# Revit family: RN 90097 Optifitt-Serra-Gewindeflansch PN 16
name_source: partatom
category: Rohrformteile
units: mm (PartAtom-declared; Revit-internal decimal feet)

## family parameters
Arbeitsebenenbasiert = Nein
Beim Laden mit Abzugskörper schneiden = Nein
Bemaßung runder Anschluss = Durchmesser verwenden
Gemeinsam genutzt = Nein
Immer vertikal = Ja
Teiletyp = Verbindung

## types (8) — shared parameters
1.010.00.2 Blattnummer der Richtlinie = 29
1.010.00.3 Ausgabedatum (Monat) der Richtlinie = 201308
1.010.00.4 Herstellername = R. Nussbaum AG
1.010.00.5 Revisionsdatum der Datei = 20190521
1.010.00.6 Webadresse des Herstellers = http://www.nussbaum.ch
1.100.00.4 Produktbezeichnung = Versorgung
1.110.00.2 Index = 3
1.110.00.4 Produktbezeichnung = Optifitt-Serra
1.960/3L.00.8 Link (URL) = https://www.nussbaum.ch
29.700.00.4 Produktname = Optifitt-Serra-Gewindeflansch PN 16
29.700.00.5 Produktkennung = 2
29.700.00.6 Querschnittsform = 1
29.700.00.7 Nennweitensystem = DN
29.700.00.8 Nenndrucksystem = PN
29.710.02.4 Nenndruck = 16
29.710.02.5 max. zul. Überdruck [hPa] = 1600
29.710.02.7 max. zul. Dauer-Betriebsdruck [hPa] = 1600
29.710.02.9 max. zul. Dauer-Betriebstemperatur [°C] = 90
Connector Visibility = Nein
EnclosingSpace Visibility = Nein
Hersteller = R. Nussbaum AG
URL = https://www.nussbaum.ch

## per-type parameters (varying)
- DN=80: 1.800.00.3 TGA-Nummer=01900300000000000000000000000000000000000000000034???000000000000008; 1.800.00.4 Kommentarfeld=90097.28, Optifitt-Serra-Gewindeflansch PN 16, DN=80, Rp=3; 1.810.00.3 Hersteller-Bestellnummer=90097.28; 1.810.00.4 DATANORM-Nummer=90097.28; 1.810.00.5 StLB-Nummer=216.641; 1.810.00.6 GTIN-Nummer=7612945680839; 29.710.02.10 Formstück-Gewicht [kg]=4.098; 29.710.02.3 Benennung=Optifitt-Serra-Gewindeflansch PN 16, DN=80, Rp=3; CONNECTOR0_DIAMETER_dX_0r=80 mm; CONNECTOR0_dX_01=30 mm; CONNECTOR0_ref_dX=30 mm; CONNECTOR1_DIAMETER_dX_0r=80 mm; CONNECTOR1_dX_00=34 mm; CONNECTOR1_dX_01=35 mm; CONNECTOR1_ref_dX=35 mm; Modell=90097.28; R. Nussbaum AG 90097.21 de Visibility=Nein; R. Nussbaum AG 90097.22 de Visibility=Nein; R. Nussbaum AG 90097.23 de Visibility=Nein; R. Nussbaum AG 90097.24 de Visibility=Nein; R. Nussbaum AG 90097.25 de Visibility=Nein; R. Nussbaum AG 90097.26 de Visibility=Nein; R. Nussbaum AG 90097.27 de Visibility=Nein; R. Nussbaum AG 90097.28 de Visibility=Ja; Typenkommentare=Optifitt-Serra-Gewindeflansch PN 16  DN=80
- DN=65: 1.800.00.3 TGA-Nummer=01900300000000000000000000000000000000000000000034???000000000000007; 1.800.00.4 Kommentarfeld=90097.27, Optifitt-Serra-Gewindeflansch PN 16, DN=65, Rp=2½; 1.810.00.3 Hersteller-Bestellnummer=90097.27; 1.810.00.4 DATANORM-Nummer=90097.27; 1.810.00.5 StLB-Nummer=216.638; 1.810.00.6 GTIN-Nummer=7612945680822; 29.710.02.10 Formstück-Gewicht [kg]=3.335; 29.710.02.3 Benennung=Optifitt-Serra-Gewindeflansch PN 16, DN=65, Rp=2½; CONNECTOR0_DIAMETER_dX_0r=65 mm; CONNECTOR0_dX_01=27 mm; CONNECTOR0_ref_dX=27 mm; CONNECTOR1_DIAMETER_dX_0r=65 mm; CONNECTOR1_dX_00=32 mm; CONNECTOR1_dX_01=33 mm; CONNECTOR1_ref_dX=33 mm; Modell=90097.27; R. Nussbaum AG 90097.21 de Visibility=Nein; R. Nussbaum AG 90097.22 de Visibility=Nein; R. Nussbaum AG 90097.23 de Visibility=Nein; R. Nussbaum AG 90097.24 de Visibility=Nein; R. Nussbaum AG 90097.25 de Visibility=Nein; R. Nussbaum AG 90097.26 de Visibility=Nein; R. Nussbaum AG 90097.27 de Visibility=Ja; R. Nussbaum AG 90097.28 de Visibility=Nein; Typenkommentare=Optifitt-Serra-Gewindeflansch PN 16  DN=65
- DN=50: 1.800.00.3 TGA-Nummer=01900300000000000000000000000000000000000000000034???000000000000006; 1.800.00.4 Kommentarfeld=90097.26, Optifitt-Serra-Gewindeflansch PN 16, DN=50, Rp=2; 1.810.00.3 Hersteller-Bestellnummer=90097.26; 1.810.00.4 DATANORM-Nummer=90097.26; 1.810.00.5 StLB-Nummer=216.637; 1.810.00.6 GTIN-Nummer=7612945680815; 29.710.02.10 Formstück-Gewicht [kg]=2.579; 29.710.02.3 Benennung=Optifitt-Serra-Gewindeflansch PN 16, DN=50, Rp=2; CONNECTOR0_DIAMETER_dX_0r=50 mm; CONNECTOR0_dX_01=24 mm; CONNECTOR0_ref_dX=24 mm; CONNECTOR1_DIAMETER_dX_0r=50 mm; CONNECTOR1_dX_00=28 mm; CONNECTOR1_dX_01=29 mm; CONNECTOR1_ref_dX=29 mm; Modell=90097.26; R. Nussbaum AG 90097.21 de Visibility=Nein; R. Nussbaum AG 90097.22 de Visibility=Nein; R. Nussbaum AG 90097.23 de Visibility=Nein; R. Nussbaum AG 90097.24 de Visibility=Nein; R. Nussbaum AG 90097.25 de Visibility=Nein; R. Nussbaum AG 90097.26 de Visibility=Ja; R. Nussbaum AG 90097.27 de Visibility=Nein; R. Nussbaum AG 90097.28 de Visibility=Nein; Typenkommentare=Optifitt-Serra-Gewindeflansch PN 16  DN=50
- DN=40: 1.800.00.3 TGA-Nummer=01900300000000000000000000000000000000000000000034???000000000000005; 1.800.00.4 Kommentarfeld=90097.25, Optifitt-Serra-Gewindeflansch PN 16, DN=40, Rp=1½; 1.810.00.3 Hersteller-Bestellnummer=90097.25; 1.810.00.4 DATANORM-Nummer=90097.25; 1.810.00.5 StLB-Nummer=216.636; 1.810.00.6 GTIN-Nummer=7612945680808; 29.710.02.10 Formstück-Gewicht [kg]=2.219; 29.710.02.3 Benennung=Optifitt-Serra-Gewindeflansch PN 16, DN=40, Rp=1½; CONNECTOR0_DIAMETER_dX_0r=40 mm; CONNECTOR0_dX_01=19 mm; CONNECTOR0_ref_dX=19 mm; CONNECTOR1_DIAMETER_dX_0r=40 mm; CONNECTOR1_dX_00=32 mm; CONNECTOR1_dX_01=33 mm; CONNECTOR1_ref_dX=33 mm; Modell=90097.25; R. Nussbaum AG 90097.21 de Visibility=Nein; R. Nussbaum AG 90097.22 de Visibility=Nein; R. Nussbaum AG 90097.23 de Visibility=Nein; R. Nussbaum AG 90097.24 de Visibility=Nein; R. Nussbaum AG 90097.25 de Visibility=Ja; R. Nussbaum AG 90097.26 de Visibility=Nein; R. Nussbaum AG 90097.27 de Visibility=Nein; R. Nussbaum AG 90097.28 de Visibility=Nein; Typenkommentare=Optifitt-Serra-Gewindeflansch PN 16  DN=40
- DN=32: 1.800.00.3 TGA-Nummer=01900300000000000000000000000000000000000000000034???000000000000004; 1.800.00.4 Kommentarfeld=90097.24, Optifitt-Serra-Gewindeflansch PN 16, DN=32, Rp=1¼; 1.810.00.3 Hersteller-Bestellnummer=90097.24; 1.810.00.4 DATANORM-Nummer=90097.24; 1.810.00.5 StLB-Nummer=216.635; 1.810.00.6 GTIN-Nummer=7612945680792; 29.710.02.10 Formstück-Gewicht [kg]=1.959; 29.710.02.3 Benennung=Optifitt-Serra-Gewindeflansch PN 16, DN=32, Rp=1¼; CONNECTOR0_DIAMETER_dX_0r=32 mm; CONNECTOR0_dX_01=19 mm; CONNECTOR0_ref_dX=19 mm; CONNECTOR1_DIAMETER_dX_0r=32 mm; CONNECTOR1_dX_00=26 mm; CONNECTOR1_dX_01=27 mm; CONNECTOR1_ref_dX=27 mm; Modell=90097.24; R. Nussbaum AG 90097.21 de Visibility=Nein; R. Nussbaum AG 90097.22 de Visibility=Nein; R. Nussbaum AG 90097.23 de Visibility=Nein; R. Nussbaum AG 90097.24 de Visibility=Ja; R. Nussbaum AG 90097.25 de Visibility=Nein; R. Nussbaum AG 90097.26 de Visibility=Nein; R. Nussbaum AG 90097.27 de Visibility=Nein; R. Nussbaum AG 90097.28 de Visibility=Nein; Typenkommentare=Optifitt-Serra-Gewindeflansch PN 16  DN=32
- DN=25: 1.800.00.3 TGA-Nummer=01900300000000000000000000000000000000000000000034???000000000000003; 1.800.00.4 Kommentarfeld=90097.23, Optifitt-Serra-Gewindeflansch PN 16, DN=25, Rp=1; 1.810.00.3 Hersteller-Bestellnummer=90097.23; 1.810.00.4 DATANORM-Nummer=90097.23; 1.810.00.5 StLB-Nummer=216.634; 1.810.00.6 GTIN-Nummer=7612945680785; 29.710.02.10 Formstück-Gewicht [kg]=1.325; 29.710.02.3 Benennung=Optifitt-Serra-Gewindeflansch PN 16, DN=25, Rp=1; CONNECTOR0_DIAMETER_dX_0r=25 mm  [stored 0.082021 ft]; CONNECTOR0_dX_01=17 mm; CONNECTOR0_ref_dX=17 mm; CONNECTOR1_DIAMETER_dX_0r=25 mm  [stored 0.082021 ft]; CONNECTOR1_dX_00=24 mm; CONNECTOR1_dX_01=25 mm  [stored 0.082021 ft]; CONNECTOR1_ref_dX=25 mm  [stored 0.082021 ft]; Modell=90097.23; R. Nussbaum AG 90097.21 de Visibility=Nein; R. Nussbaum AG 90097.22 de Visibility=Nein; R. Nussbaum AG 90097.23 de Visibility=Ja; R. Nussbaum AG 90097.24 de Visibility=Nein; R. Nussbaum AG 90097.25 de Visibility=Nein; R. Nussbaum AG 90097.26 de Visibility=Nein; R. Nussbaum AG 90097.27 de Visibility=Nein; R. Nussbaum AG 90097.28 de Visibility=Nein; Typenkommentare=Optifitt-Serra-Gewindeflansch PN 16  DN=25
- DN=20: 1.800.00.3 TGA-Nummer=01900300000000000000000000000000000000000000000034???000000000000002; 1.800.00.4 Kommentarfeld=90097.22, Optifitt-Serra-Gewindeflansch PN 16, DN=20, Rp=¾; 1.810.00.3 Hersteller-Bestellnummer=90097.22; 1.810.00.4 DATANORM-Nummer=90097.22; 1.810.00.5 StLB-Nummer=216.633; 1.810.00.6 GTIN-Nummer=7612945680778; 29.710.02.10 Formstück-Gewicht [kg]=0.929; 29.710.02.3 Benennung=Optifitt-Serra-Gewindeflansch PN 16, DN=20, Rp=¾; CONNECTOR0_DIAMETER_dX_0r=20 mm; CONNECTOR0_dX_01=15 mm; CONNECTOR0_ref_dX=15 mm; CONNECTOR1_DIAMETER_dX_0r=20 mm; CONNECTOR1_dX_00=24 mm; CONNECTOR1_dX_01=25 mm  [stored 0.082021 ft]; CONNECTOR1_ref_dX=25 mm  [stored 0.082021 ft]; Modell=90097.22; R. Nussbaum AG 90097.21 de Visibility=Nein; R. Nussbaum AG 90097.22 de Visibility=Ja; R. Nussbaum AG 90097.23 de Visibility=Nein; R. Nussbaum AG 90097.24 de Visibility=Nein; R. Nussbaum AG 90097.25 de Visibility=Nein; R. Nussbaum AG 90097.26 de Visibility=Nein; R. Nussbaum AG 90097.27 de Visibility=Nein; R. Nussbaum AG 90097.28 de Visibility=Nein; Typenkommentare=Optifitt-Serra-Gewindeflansch PN 16  DN=20
- DN=15: 1.800.00.3 TGA-Nummer=01900300000000000000000000000000000000000000000034???000000000000001; 1.800.00.4 Kommentarfeld=90097.21, Optifitt-Serra-Gewindeflansch PN 16, DN=15, Rp=½; 1.810.00.3 Hersteller-Bestellnummer=90097.21; 1.810.00.4 DATANORM-Nummer=90097.21; 1.810.00.5 StLB-Nummer=216.632; 1.810.00.6 GTIN-Nummer=7612945680761; 29.710.02.10 Formstück-Gewicht [kg]=0.779; 29.710.02.3 Benennung=Optifitt-Serra-Gewindeflansch PN 16, DN=15, Rp=½; CONNECTOR0_DIAMETER_dX_0r=15 mm; CONNECTOR0_dX_01=13 mm; CONNECTOR0_ref_dX=13 mm; CONNECTOR1_DIAMETER_dX_0r=15 mm; CONNECTOR1_dX_00=20 mm; CONNECTOR1_dX_01=21 mm; CONNECTOR1_ref_dX=21 mm; Modell=90097.21; R. Nussbaum AG 90097.21 de Visibility=Ja; R. Nussbaum AG 90097.22 de Visibility=Nein; R. Nussbaum AG 90097.23 de Visibility=Nein; R. Nussbaum AG 90097.24 de Visibility=Nein; R. Nussbaum AG 90097.25 de Visibility=Nein; R. Nussbaum AG 90097.26 de Visibility=Nein; R. Nussbaum AG 90097.27 de Visibility=Nein; R. Nussbaum AG 90097.28 de Visibility=Nein; Typenkommentare=Optifitt-Serra-Gewindeflansch PN 16  DN=15

note: [stored X ft] marks values corroborated as IEEE doubles in the binary element streams (Revit-internal decimal feet)

## geometry (parser evidence)
native form markers: Sweep x2
no freeform markers — native parametric forms only
